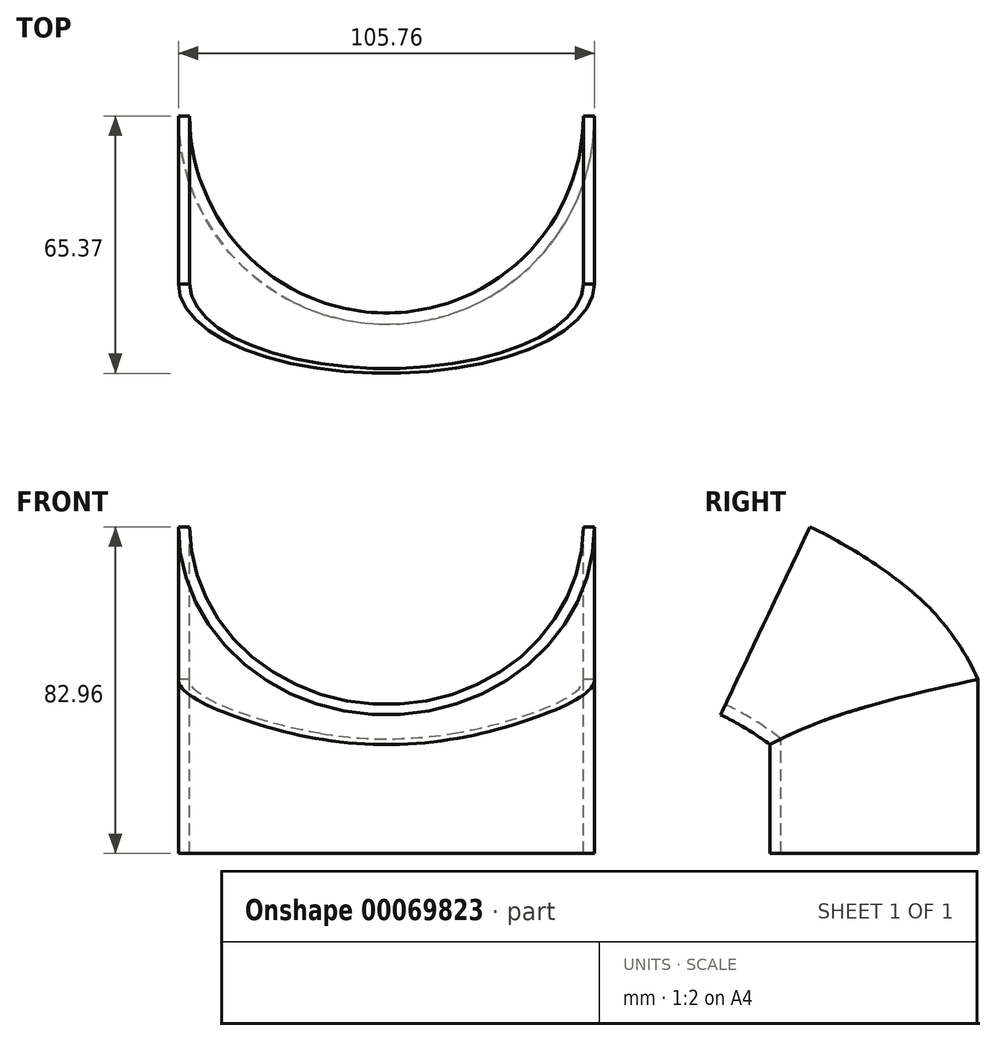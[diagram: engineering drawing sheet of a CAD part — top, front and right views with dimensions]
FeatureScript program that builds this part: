
annotation { "Feature Type Name" : "Feature", "Feature Type Description" : "" }
export const myFeature = defineFeature(function(context is Context, id is Id, definition is map)
    precondition{}
    {
        {
            var Q0;
            Q0=qCreatedBy(makeId("Top.planeOp"),FACE);
            var sketch = newSketch(context, id + "F0", { "sketchPlane" : qUnion([Q0])});
            skArc(sketch, "E0", {"start": v(-50, 0) * mm, "mid": v(0, -50) * mm, "end": v(50, 0) * mm});
            skArc(sketch, "E1.0", {"start": v(-52.88, 0) * mm, "mid": v(0, -52.88) * mm, "end": v(52.88, 0) * mm});
            skLineSegment(sketch, "E2", {"start": v(-52.88, 0) * mm, "end": v(-50, 0) * mm});
            skLineSegment(sketch, "E3", {"start": v(50, 0) * mm, "end": v(52.88, 0) * mm});
            skSolve(sketch);
        }
        {
            var Q0;
            Q0=qCreatedBy(makeId("Right.planeOp"),FACE);
            var sketch = newSketch(context, id + "F1", { "sketchPlane" : qUnion([Q0])});
            skLineSegment(sketch, "E4.0", {"start": v(-52.88, 0) * mm, "end": v(0, 0) * mm});
            skLineSegment(sketch, "E5", {"start": v(-52.88, 0) * mm, "end": v(-52.88, 11.89) * mm});
            skArc(sketch, "E6", {"start": v(-52.88, 11.89) * mm, "mid": v(-47.8, 18.4) * mm, "end": v(-50.85, 26.08) * mm});
            skArc(sketch, "E7", {"start": v(-50.85, 26.08) * mm, "mid": v(-57.84, 31.08) * mm, "end": v(-65.37, 35.22) * mm});
            skSolve(sketch);
        }
        {
            var Q0;
            Q0=makeQuery(id+"F0.imprint","IMPRINT",FACE,{"disambiguationData":[TD([[makeQuery(id+"F0.imprint","IMPRINT",EDGE,{"derivedFrom":sQuery(id+"F0.wireOp",EDGE,"E0")}),-1.0]])]});
            var Q1;
            Q1=sQuery(id+"F1.wireOp",EDGE,"E5");
            var Q2;
            Q2=sQuery(id+"F1.wireOp",EDGE,"E6");
            var Q3;
            Q3=sQuery(id+"F1.wireOp",EDGE,"E7");
            sweep(context, id + "F2", {"profiles" : qUnion([Q0]), "path" : qUnion([Q1, Q2, Q3])});
        }
    });
